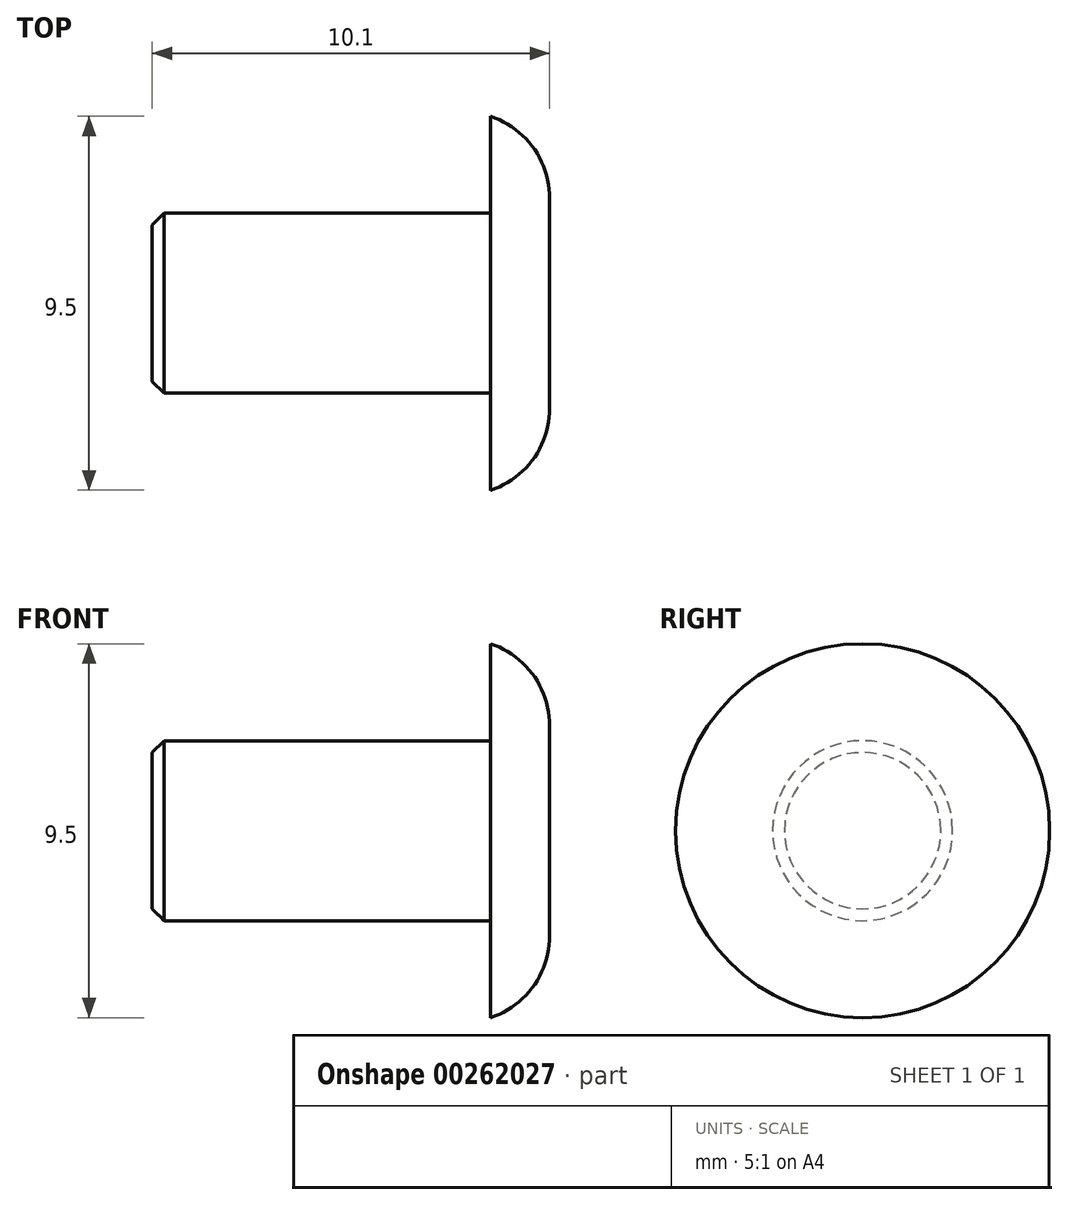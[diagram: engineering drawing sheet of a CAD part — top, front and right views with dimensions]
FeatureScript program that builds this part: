
annotation { "Feature Type Name" : "Feature", "Feature Type Description" : "" }
export const myFeature = defineFeature(function(context is Context, id is Id, definition is map)
    precondition{}
    {
        {
            assignVariable(context, id + "F0", {"name" : "WrenchSize", "anyValue" : 9.5});
        }
        {
            assignVariable(context, id + "F1", {"name" : "HeadDepth", "anyValue" : 1.5});
        }
        {
            assignVariable(context, id + "F2", {"name" : "ThreadLength", "anyValue" : 6.35});
        }
        {
            assignVariable(context, id + "F3", {"name" : "SL", "anyValue" : getVariable(context, 'ThreadLength') + (getVariable(context, 'HeadDepth') * 2)});
        }
        {
            var Q0;
            Q0=qCreatedBy(makeId("Front.planeOp"),FACE);
            var sketch = newSketch(context, id + "F4", { "sketchPlane" : qUnion([Q0])});
            skLineSegment(sketch, "E0", {"start": v(-45.65, 0) * mm, "end": v(59.4, 0) * mm, "construction": true});
            skSolve(sketch);
        }
        {
            var Q0;
            Q0=qCreatedBy(makeId("Right.planeOp"),FACE);
            var sketch = newSketch(context, id + "F5", { "sketchPlane" : qUnion([Q0])});
            skCircle(sketch, "E1", {"center": v(0, 0) * mm, "radius": 2.29 * mm});
            skSolve(sketch);
        }
        {
            var Q0;
            Q0=qCreatedBy(makeId("Right.planeOp"),FACE);
            var sketch = newSketch(context, id + "F6", { "sketchPlane" : qUnion([Q0])});
            skCircle(sketch, "E2", {"center": v(0, 0) * mm, "radius": 2.29 * mm});
            skSolve(sketch);
        }
        {
            var Q0;
            Q0=qSketchRegion(id+"F5",true);
            var Q1;
            Q1=qSketchRegion(id+"FMsuZWWzzBI7FA4_0",true);
            var Q2;
            Q2=qConstructionFilter(qBodyType(qCreatedBy(id+"F5",EDGE),BodyType.WIRE),ConstructionObject.NO);
            extrude(context, id + "F7", {"entities" : qUnion([Q0, Q1]), "bodyType" : ExtendedToolBodyType.SURFACE, "surfaceEntities" : qUnion([Q2]), "oppositeDirection" : true, "depth" : (getVariable(context, 'SL') * 1.1) * mm});
        }
        {
            var Q0;
            Q0=makeQuery(id+"F6.imprint","IMPRINT",FACE,{"disambiguationData":[TD([[makeQuery(id+"F6.imprint","IMPRINT",EDGE,{"derivedFrom":sQuery(id+"F6.wireOp",EDGE,"E2")}),1.0]])]});
            extrude(context, id + "F8", {"entities" : qUnion([Q0]), "oppositeDirection" : true, "depth" : (getVariable(context, 'SL')) * mm});
        }
        {
            var Q0;
            Q0=makeQuery(id+"F8.opExtrude","CAP_FACE",FACE,{"disambiguationData":[OSD([sQuery(id+"F6.wireOp",EDGE,"E2")])],"isStart":false});
            chamfer(context, id + "F9", {"entities" : qUnion([Q0]), "width" : (0.2 * getVariable(context, 'HeadDepth')) * mm, "tangentPropagation" : true});
        }
        {
            var Q0;
            Q0=qCreatedBy(makeId("Right.planeOp"),FACE);
            var sketch = newSketch(context, id + "F10", { "sketchPlane" : qUnion([Q0])});
            skCircle(sketch, "E3.cCircle", {"center": v(0, 0) * mm, "radius": 4.75 * mm});
            skLineSegment(sketch, "E3.0", {"start": v(-0.07, 5.48) * mm, "end": v(4.72, 2.8) * mm, "construction": true});
            skLineSegment(sketch, "E3.1", {"start": v(4.72, 2.8) * mm, "end": v(4.78, -2.69) * mm, "construction": true});
            skLineSegment(sketch, "E3.2", {"start": v(4.78, -2.69) * mm, "end": v(0.07, -5.48) * mm, "construction": true});
            skLineSegment(sketch, "E3.3", {"start": v(0.07, -5.48) * mm, "end": v(-4.72, -2.8) * mm, "construction": true});
            skLineSegment(sketch, "E3.4", {"start": v(-4.72, -2.8) * mm, "end": v(-4.78, 2.69) * mm, "construction": true});
            skLineSegment(sketch, "E3.5", {"start": v(-4.78, 2.69) * mm, "end": v(-0.07, 5.48) * mm, "construction": true});
            skPoint(sketch, "E3.0.midPoint", {"position": v(2.33, 4.14) * mm});
            skSolve(sketch);
        }
        {
            var Q0;
            Q0=makeQuery(id+"F10.imprint","IMPRINT",FACE,{"disambiguationData":[TD([[makeQuery(id+"F10.imprint","IMPRINT",EDGE,{"derivedFrom":sQuery(id+"F10.wireOp",EDGE,"E3.cCircle")}),1.0]])]});
            extrude(context, id + "F11", {"entities" : qUnion([Q0]), "operationType" : NewBodyOperationType.ADD, "depth" : (getVariable(context, 'HeadDepth') / 2) * mm, "hasSecondDirection" : true, "secondDirectionOppositeDirection" : true, "secondDirectionDepth" : (getVariable(context, 'HeadDepth') / 2) * mm});
        }
        {
            var Q0;
            Q0=makeQuery(id+"F11.opExtrude","CAP_EDGE",EDGE,{"disambiguationData":[OSD([sQuery(id+"F10.wireOp",EDGE,"E3.cCircle")])],"isStart":false});
            fillet(context, id + "F12", {"entities" : qUnion([Q0]), "radius" : (getVariable(context, 'WrenchSize') + getVariable(context, 'HeadDepth')) / 5 * mm, "tangentPropagation" : true, "allowEdgeOverflow" : false});
        }
        {
            var Q0;
            Q0=makeQuery(id+"F7.opExtrude","SWEPT_BODY",BODY,{"disambiguationData":[OSD([sQuery(id+"F5.wireOp",EDGE,"E1")])]});
            deleteBodies(context, id + "F13", {"entities" : qUnion([Q0])});
        }
    });
